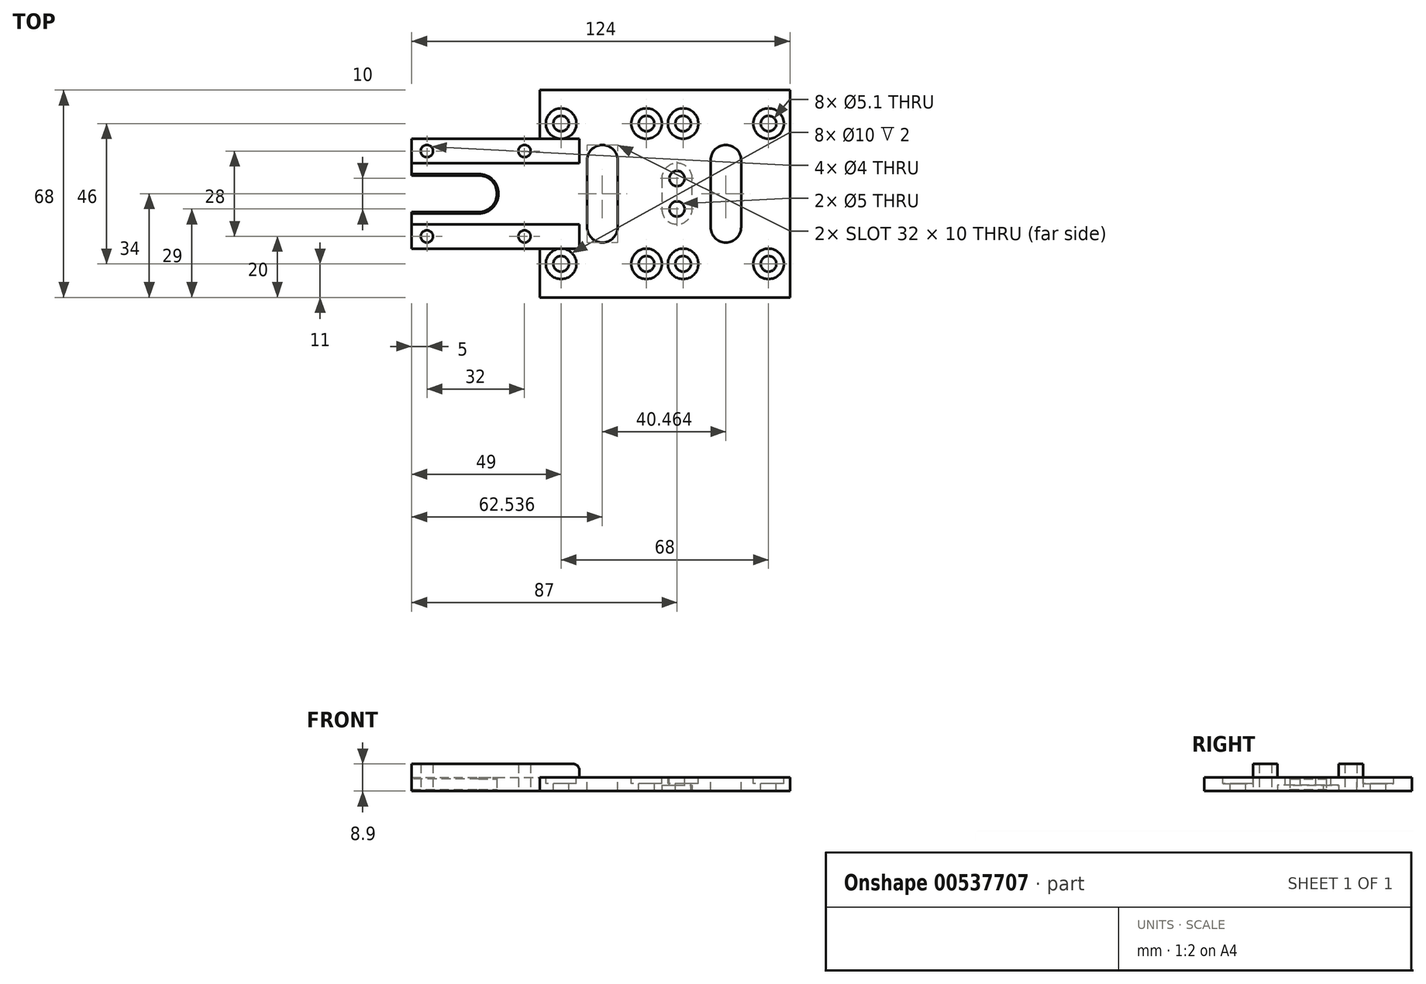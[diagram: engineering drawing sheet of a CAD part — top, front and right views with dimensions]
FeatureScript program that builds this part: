
annotation { "Feature Type Name" : "Feature", "Feature Type Description" : "" }
export const myFeature = defineFeature(function(context is Context, id is Id, definition is map)
    precondition{}
    {
        {
            var Q0;
            Q0=qCreatedBy(makeId("Top.planeOp"),FACE);
            var sketch = newSketch(context, id + "F0", { "sketchPlane" : qUnion([Q0])});
            skLineSegment(sketch, "E0.bottom", {"start": v(0, 0) * mm, "end": v(82, 0) * mm});
            skLineSegment(sketch, "E0.top", {"start": v(0, 68) * mm, "end": v(82, 68) * mm});
            skLineSegment(sketch, "E0.left", {"start": v(0, 0) * mm, "end": v(0, 16) * mm});
            skLineSegment(sketch, "E0.right", {"start": v(82, 0) * mm, "end": v(82, 68) * mm});
            skLineSegment(sketch, "E1.bottom", {"start": v(0, 52) * mm, "end": v(-42, 52) * mm});
            skLineSegment(sketch, "E1.top", {"start": v(0, 16) * mm, "end": v(-42, 16) * mm});
            skLineSegment(sketch, "E1.right", {"start": v(-42, 52) * mm, "end": v(-42, 40) * mm});
            skArc(sketch, "E2", {"start": v(-20.02, 28) * mm, "mid": v(-14.02, 34) * mm, "end": v(-20.02, 40) * mm});
            skLineSegment(sketch, "E3.bottom", {"start": v(-20.02, 40) * mm, "end": v(-42, 40) * mm});
            skLineSegment(sketch, "E3.top", {"start": v(-20.02, 28) * mm, "end": v(-42, 28) * mm});
            skLineSegment(sketch, "E3.left", {"start": v(-20.02, 28) * mm, "end": v(-20.02, 28) * mm});
            skLineSegment(sketch, "E4.trimOffspring", {"start": v(0, 52) * mm, "end": v(0, 68) * mm});
            skLineSegment(sketch, "E5.trimOffspring", {"start": v(-42, 28) * mm, "end": v(-42, 16) * mm});
            skSolve(sketch);
        }
        {
            var Q0;
            Q0=makeQuery(id+"F0.imprint","IMPRINT",FACE,{"disambiguationData":[TD([[makeQuery(id+"F0.imprint","IMPRINT",EDGE,{"derivedFrom":sQuery(id+"F0.wireOp",EDGE,"E0.bottom")}),1.0]])]});
            extrude(context, id + "F1", {"entities" : qUnion([Q0]), "depth" : 4.5 * mm, "offsetDistance" : 25 * mm});
        }
        {
            var Q0;
            Q0=makeQuery(id+"F1.opExtrude","CAP_FACE",FACE,{"disambiguationData":[OSD([sQuery(id+"F0.wireOp",EDGE,"E0.bottom"),sQuery(id+"F0.wireOp",EDGE,"E0.top"),sQuery(id+"F0.wireOp",EDGE,"E0.left"),sQuery(id+"F0.wireOp",EDGE,"E0.right"),sQuery(id+"F0.wireOp",EDGE,"E1.bottom"),sQuery(id+"F0.wireOp",EDGE,"E1.top"),sQuery(id+"F0.wireOp",EDGE,"E1.right"),sQuery(id+"F0.wireOp",EDGE,"E2"),sQuery(id+"F0.wireOp",EDGE,"E3.bottom"),sQuery(id+"F0.wireOp",EDGE,"E3.top"),sQuery(id+"F0.wireOp",EDGE,"E3.left"),sQuery(id+"F0.wireOp",EDGE,"E4.trimOffspring"),sQuery(id+"F0.wireOp",EDGE,"E5.trimOffspring")])],"isStart":false});
            var sketch = newSketch(context, id + "F2", { "sketchPlane" : qUnion([Q0])});
            skCircle(sketch, "E6", {"center": v(75, 57) * mm, "radius": 2.55 * mm});
            skCircle(sketch, "E7", {"center": v(75, 11) * mm, "radius": 2.55 * mm});
            skCircle(sketch, "E8", {"center": v(47, 57) * mm, "radius": 2.55 * mm});
            skCircle(sketch, "E9", {"center": v(47, 11) * mm, "radius": 2.55 * mm});
            skCircle(sketch, "E10", {"center": v(35, 57) * mm, "radius": 2.55 * mm});
            skCircle(sketch, "E11", {"center": v(35, 11) * mm, "radius": 2.55 * mm});
            skCircle(sketch, "E12", {"center": v(7, 57) * mm, "radius": 2.55 * mm});
            skCircle(sketch, "E13", {"center": v(7, 11) * mm, "radius": 2.55 * mm});
            skSolve(sketch);
        }
        {
            var Q0;
            Q0 = qSketchRegion(id + "F2", true);
            extrude(context, id + "F3", {"entities" : qUnion([Q0]), "operationType" : NewBodyOperationType.REMOVE, "oppositeDirection" : true, "depth" : 25 * mm, "offsetDistance" : 25 * mm});
        }
        {
            var Q0;
            Q0=makeQuery(id+"F1.opExtrude","CAP_FACE",FACE,{"disambiguationData":[OSD([sQuery(id+"F0.wireOp",EDGE,"E0.bottom"),sQuery(id+"F0.wireOp",EDGE,"E0.top"),sQuery(id+"F0.wireOp",EDGE,"E0.left"),sQuery(id+"F0.wireOp",EDGE,"E0.right"),sQuery(id+"F0.wireOp",EDGE,"E1.bottom"),sQuery(id+"F0.wireOp",EDGE,"E1.top"),sQuery(id+"F0.wireOp",EDGE,"E1.right"),sQuery(id+"F0.wireOp",EDGE,"E2"),sQuery(id+"F0.wireOp",EDGE,"E3.bottom"),sQuery(id+"F0.wireOp",EDGE,"E3.top"),sQuery(id+"F0.wireOp",EDGE,"E3.left"),sQuery(id+"F0.wireOp",EDGE,"E4.trimOffspring"),sQuery(id+"F0.wireOp",EDGE,"E5.trimOffspring")])],"isStart":false});
            var sketch = newSketch(context, id + "F4", { "sketchPlane" : qUnion([Q0])});
            skLineSegment(sketch, "E14.bottom", {"start": v(-42, 52) * mm, "end": v(13, 52) * mm});
            skLineSegment(sketch, "E14.top", {"start": v(-42, 44) * mm, "end": v(13, 44) * mm});
            skLineSegment(sketch, "E14.left", {"start": v(-42, 52) * mm, "end": v(-42, 44) * mm});
            skLineSegment(sketch, "E14.right", {"start": v(13, 52) * mm, "end": v(13, 44) * mm});
            skPoint(sketch, "E15.oppositeSnap0", {"position": v(-45, 24) * mm});
            skLineSegment(sketch, "E15.bottom", {"start": v(-42, 16) * mm, "end": v(13, 16) * mm});
            skLineSegment(sketch, "E15.top", {"start": v(-42, 24) * mm, "end": v(13, 24) * mm});
            skLineSegment(sketch, "E15.left", {"start": v(-42, 16) * mm, "end": v(-42, 24) * mm});
            skLineSegment(sketch, "E15.right", {"start": v(13, 16) * mm, "end": v(13, 24) * mm});
            skSolve(sketch);
        }
        {
            var Q0;
            Q0 = qSketchRegion(id + "F4", true);
            extrude(context, id + "F5", {"entities" : qUnion([Q0]), "operationType" : NewBodyOperationType.ADD, "depth" : 4.4 * mm, "offsetDistance" : 25 * mm});
        }
        {
            var Q0;
            {var subQ2=sQuery(id+"F0.wireOp",EDGE,"E5.trimOffspring");var subQ3=sQuery(id+"F0.wireOp",EDGE,"E3.left");var subQ4=sQuery(id+"F0.wireOp",EDGE,"E3.top");var subQ5=sQuery(id+"F0.wireOp",EDGE,"E0.right");var subQ6=sQuery(id+"F0.wireOp",EDGE,"E3.bottom");var subQ7=sQuery(id+"F0.wireOp",EDGE,"E1.right");var subQ8=sQuery(id+"F0.wireOp",EDGE,"E2");Q0=makeQuery(id+"F5.boolean.opBoolean","SPLIT",FACE,{"disambiguationData":[TD([makeQuery(id+"F1.opExtrude","SWEPT_FACE",FACE,{"disambiguationData":[OSD([subQ7])]})])],"derivedFrom":makeQuery(id+"F1.opExtrude","CAP_FACE",FACE,{"disambiguationData":[OSD([sQuery(id+"F0.wireOp",EDGE,"E0.bottom"),sQuery(id+"F0.wireOp",EDGE,"E0.top"),sQuery(id+"F0.wireOp",EDGE,"E0.left"),subQ5,sQuery(id+"F0.wireOp",EDGE,"E1.bottom"),sQuery(id+"F0.wireOp",EDGE,"E1.top"),subQ7,subQ8,subQ6,subQ4,subQ3,sQuery(id+"F0.wireOp",EDGE,"E4.trimOffspring"),subQ2])],"isStart":false})});}
            var sketch = newSketch(context, id + "F6", { "sketchPlane" : qUnion([Q0])});
            skCircle(sketch, "E16", {"center": v(45, 29) * mm, "radius": 2.5 * mm});
            skCircle(sketch, "E17", {"center": v(45, 39) * mm, "radius": 2.5 * mm});
            skSolve(sketch);
        }
        {
            var Q0;
            Q0 = qSketchRegion(id + "F6", true);
            extrude(context, id + "F7", {"entities" : qUnion([Q0]), "operationType" : NewBodyOperationType.REMOVE, "oppositeDirection" : true, "depth" : 25 * mm, "offsetDistance" : 25 * mm});
        }
        {
            var Q0;
            Q0=makeQuery(id+"F1.opExtrude","CAP_FACE",FACE,{"disambiguationData":[OSD([sQuery(id+"F0.wireOp",EDGE,"E0.bottom"),sQuery(id+"F0.wireOp",EDGE,"E0.top"),sQuery(id+"F0.wireOp",EDGE,"E0.left"),sQuery(id+"F0.wireOp",EDGE,"E0.right"),sQuery(id+"F0.wireOp",EDGE,"E1.bottom"),sQuery(id+"F0.wireOp",EDGE,"E1.top"),sQuery(id+"F0.wireOp",EDGE,"E1.right"),sQuery(id+"F0.wireOp",EDGE,"E2"),sQuery(id+"F0.wireOp",EDGE,"E3.bottom"),sQuery(id+"F0.wireOp",EDGE,"E3.top"),sQuery(id+"F0.wireOp",EDGE,"E4.trimOffspring"),sQuery(id+"F0.wireOp",EDGE,"E5.trimOffspring")])],"isStart":true});
            var sketch = newSketch(context, id + "F8", { "sketchPlane" : qUnion([Q0])});
            skCircle(sketch, "E18", {"center": v(-37, -48) * mm, "radius": 2 * mm});
            skCircle(sketch, "E19", {"center": v(-5, -48) * mm, "radius": 2 * mm});
            skCircle(sketch, "E20", {"center": v(-37, -20) * mm, "radius": 2 * mm});
            skCircle(sketch, "E21", {"center": v(-5, -20) * mm, "radius": 2 * mm});
            skSolve(sketch);
        }
        {
            var Q0;
            Q0 = qSketchRegion(id + "F8", true);
            extrude(context, id + "F9", {"entities" : qUnion([Q0]), "operationType" : NewBodyOperationType.REMOVE, "oppositeDirection" : true, "depth" : 25 * mm, "offsetDistance" : 25 * mm});
        }
        {
            var Q0;
            Q0=makeQuery(id+"F1.opExtrude","CAP_FACE",FACE,{"disambiguationData":[OSD([sQuery(id+"F0.wireOp",EDGE,"E0.bottom"),sQuery(id+"F0.wireOp",EDGE,"E0.top"),sQuery(id+"F0.wireOp",EDGE,"E0.left"),sQuery(id+"F0.wireOp",EDGE,"E0.right"),sQuery(id+"F0.wireOp",EDGE,"E1.bottom"),sQuery(id+"F0.wireOp",EDGE,"E1.top"),sQuery(id+"F0.wireOp",EDGE,"E1.right"),sQuery(id+"F0.wireOp",EDGE,"E2"),sQuery(id+"F0.wireOp",EDGE,"E3.bottom"),sQuery(id+"F0.wireOp",EDGE,"E3.top"),sQuery(id+"F0.wireOp",EDGE,"E4.trimOffspring"),sQuery(id+"F0.wireOp",EDGE,"E5.trimOffspring")])],"isStart":false});
            var sketch = newSketch(context, id + "F10", { "sketchPlane" : qUnion([Q0])});
            skLineSegment(sketch, "E22.bottom", {"start": v(56, 50) * mm, "end": v(66, 50) * mm});
            skLineSegment(sketch, "E22.top", {"start": v(56, 18) * mm, "end": v(66, 18) * mm});
            skLineSegment(sketch, "E22.left", {"start": v(56, 50) * mm, "end": v(56, 18) * mm});
            skLineSegment(sketch, "E22.right", {"start": v(66, 50) * mm, "end": v(66, 18) * mm});
            skLineSegment(sketch, "E23.bottom", {"start": v(15.54, 50) * mm, "end": v(25.54, 50) * mm});
            skLineSegment(sketch, "E23.top", {"start": v(15.54, 18) * mm, "end": v(25.54, 18) * mm});
            skLineSegment(sketch, "E23.left", {"start": v(15.54, 50) * mm, "end": v(15.54, 18) * mm});
            skLineSegment(sketch, "E23.right", {"start": v(25.54, 50) * mm, "end": v(25.54, 18) * mm});
            skSolve(sketch);
        }
        {
            var Q0;
            Q0 = qSketchRegion(id + "F10", true);
            extrude(context, id + "F11", {"entities" : qUnion([Q0]), "operationType" : NewBodyOperationType.REMOVE, "oppositeDirection" : true, "depth" : 25 * mm, "offsetDistance" : 25 * mm});
        }
        {
            var Q0;
            Q0=makeQuery(id+"F11.boolean.opBoolean","COPY",EDGE,{"derivedFrom":makeQuery(id+"F11.opExtrude","SWEPT_EDGE",EDGE,{"disambiguationData":[OSD([sQuery(id+"F4.wireOp",EDGE,"E14.right"),sQuery(id+"F10.wireOp",EDGE,"E23.bottom"),sQuery(id+"F10.wireOp",EDGE,"E23.left")])]})});
            var Q1;
            Q1=makeQuery(id+"F11.boolean.opBoolean","COPY",EDGE,{"derivedFrom":makeQuery(id+"F11.opExtrude","SWEPT_EDGE",EDGE,{"disambiguationData":[OSD([sQuery(id+"F10.wireOp",EDGE,"E23.bottom"),sQuery(id+"F10.wireOp",EDGE,"E23.right")])]})});
            var Q2;
            Q2=makeQuery(id+"F11.boolean.opBoolean","COPY",EDGE,{"derivedFrom":makeQuery(id+"F11.opExtrude","SWEPT_EDGE",EDGE,{"disambiguationData":[OSD([sQuery(id+"F4.wireOp",EDGE,"E15.right"),sQuery(id+"F10.wireOp",EDGE,"E23.top"),sQuery(id+"F10.wireOp",EDGE,"E23.left")])]})});
            var Q3;
            Q3=makeQuery(id+"F11.boolean.opBoolean","COPY",EDGE,{"derivedFrom":makeQuery(id+"F11.opExtrude","SWEPT_EDGE",EDGE,{"disambiguationData":[OSD([sQuery(id+"F10.wireOp",EDGE,"E23.top"),sQuery(id+"F10.wireOp",EDGE,"E23.right")])]})});
            fillet(context, id + "F12", {"entities" : qUnion([Q0, Q1, Q2, Q3]), "radius" : 5 * mm, "tangentPropagation" : true, "allowEdgeOverflow" : false});
        }
        {
            var Q0;
            Q0=makeQuery(id+"F11.boolean.opBoolean","COPY",EDGE,{"derivedFrom":makeQuery(id+"F11.opExtrude","SWEPT_EDGE",EDGE,{"disambiguationData":[OSD([sQuery(id+"F10.wireOp",EDGE,"E22.top"),sQuery(id+"F10.wireOp",EDGE,"E22.left")])]})});
            var Q1;
            Q1=makeQuery(id+"F11.boolean.opBoolean","COPY",EDGE,{"derivedFrom":makeQuery(id+"F11.opExtrude","SWEPT_EDGE",EDGE,{"disambiguationData":[OSD([sQuery(id+"F10.wireOp",EDGE,"E22.top"),sQuery(id+"F10.wireOp",EDGE,"E22.right")])]})});
            var Q2;
            Q2=makeQuery(id+"F11.boolean.opBoolean","COPY",EDGE,{"derivedFrom":makeQuery(id+"F11.opExtrude","SWEPT_EDGE",EDGE,{"disambiguationData":[OSD([sQuery(id+"F10.wireOp",EDGE,"E22.bottom"),sQuery(id+"F10.wireOp",EDGE,"E22.right")])]})});
            var Q3;
            Q3=makeQuery(id+"F11.boolean.opBoolean","COPY",EDGE,{"derivedFrom":makeQuery(id+"F11.opExtrude","SWEPT_EDGE",EDGE,{"disambiguationData":[OSD([sQuery(id+"F10.wireOp",EDGE,"E22.bottom"),sQuery(id+"F10.wireOp",EDGE,"E22.left")])]})});
            fillet(context, id + "F13", {"entities" : qUnion([Q0, Q1, Q2, Q3]), "radius" : 5 * mm, "tangentPropagation" : true, "allowEdgeOverflow" : false});
        }
        {
            var Q0;
            Q0=makeQuery(id+"F5.opExtrude","CAP_EDGE",EDGE,{"disambiguationData":[OSD([sQuery(id+"F4.wireOp",EDGE,"E14.right")])],"isStart":false});
            var Q1;
            Q1=makeQuery(id+"F5.opExtrude","CAP_EDGE",EDGE,{"disambiguationData":[OSD([sQuery(id+"F4.wireOp",EDGE,"E15.right")])],"isStart":false});
            fillet(context, id + "F14", {"entities" : qUnion([Q0, Q1]), "radius" : 2 * mm, "tangentPropagation" : true, "allowEdgeOverflow" : false});
        }
        {
            var Q0;
            Q0=makeQuery(id+"F1.opExtrude","CAP_FACE",FACE,{"disambiguationData":[OSD([sQuery(id+"F0.wireOp",EDGE,"E0.bottom"),sQuery(id+"F0.wireOp",EDGE,"E0.top"),sQuery(id+"F0.wireOp",EDGE,"E0.left"),sQuery(id+"F0.wireOp",EDGE,"E0.right"),sQuery(id+"F0.wireOp",EDGE,"E1.bottom"),sQuery(id+"F0.wireOp",EDGE,"E1.top"),sQuery(id+"F0.wireOp",EDGE,"E1.right"),sQuery(id+"F0.wireOp",EDGE,"E2"),sQuery(id+"F0.wireOp",EDGE,"E3.bottom"),sQuery(id+"F0.wireOp",EDGE,"E3.top"),sQuery(id+"F0.wireOp",EDGE,"E4.trimOffspring"),sQuery(id+"F0.wireOp",EDGE,"E5.trimOffspring")])],"isStart":false});
            var sketch = newSketch(context, id + "F15", { "sketchPlane" : qUnion([Q0])});
            skCircle(sketch, "E24", {"center": v(75, 11) * mm, "radius": 5 * mm});
            skCircle(sketch, "E25", {"center": v(47, 11) * mm, "radius": 5 * mm});
            skCircle(sketch, "E26", {"center": v(35, 11) * mm, "radius": 5 * mm});
            skCircle(sketch, "E27", {"center": v(7, 11) * mm, "radius": 5 * mm});
            skCircle(sketch, "E28", {"center": v(7, 57) * mm, "radius": 5 * mm});
            skCircle(sketch, "E29", {"center": v(35, 57) * mm, "radius": 5 * mm});
            skCircle(sketch, "E30", {"center": v(47, 57) * mm, "radius": 5 * mm});
            skCircle(sketch, "E31", {"center": v(75, 57) * mm, "radius": 5 * mm});
            skSolve(sketch);
        }
        {
            var Q0;
            Q0 = qSketchRegion(id + "F15", true);
            extrude(context, id + "F16", {"entities" : qUnion([Q0]), "operationType" : NewBodyOperationType.REMOVE, "oppositeDirection" : true, "depth" : 2 * mm, "offsetDistance" : 25 * mm});
        }
        {
            var Q0;
            Q0=makeQuery(id+"F1.opExtrude","CAP_FACE",FACE,{"disambiguationData":[OSD([sQuery(id+"F0.wireOp",EDGE,"E0.bottom"),sQuery(id+"F0.wireOp",EDGE,"E0.top"),sQuery(id+"F0.wireOp",EDGE,"E0.left"),sQuery(id+"F0.wireOp",EDGE,"E0.right"),sQuery(id+"F0.wireOp",EDGE,"E1.bottom"),sQuery(id+"F0.wireOp",EDGE,"E1.top"),sQuery(id+"F0.wireOp",EDGE,"E1.right"),sQuery(id+"F0.wireOp",EDGE,"E2"),sQuery(id+"F0.wireOp",EDGE,"E3.bottom"),sQuery(id+"F0.wireOp",EDGE,"E3.top"),sQuery(id+"F0.wireOp",EDGE,"E4.trimOffspring"),sQuery(id+"F0.wireOp",EDGE,"E5.trimOffspring")])],"isStart":true});
            var sketch = newSketch(context, id + "F17", { "sketchPlane" : qUnion([Q0])});
            skArc(sketch, "E32", {"start": v(40, -38.91) * mm, "mid": v(44.96, -44) * mm, "end": v(50, -39) * mm});
            skArc(sketch, "E33", {"start": v(50, -29) * mm, "mid": v(45, -24) * mm, "end": v(40, -29) * mm});
            skLineSegment(sketch, "E34", {"start": v(40, -39.09) * mm, "end": v(40, -29) * mm});
            skLineSegment(sketch, "E35", {"start": v(50, -29) * mm, "end": v(50, -39) * mm});
            skSolve(sketch);
        }
        {
            var Q0;
            Q0 = qSketchRegion(id + "F17", true);
            extrude(context, id + "F18", {"entities" : qUnion([Q0]), "operationType" : NewBodyOperationType.REMOVE, "oppositeDirection" : true, "depth" : 2 * mm, "offsetDistance" : 25 * mm});
        }
        {
            var Q0;
            Q0=makeQuery(id+"F1.opExtrude","CAP_EDGE",EDGE,{"disambiguationData":[OSD([sQuery(id+"F0.wireOp",EDGE,"E3.top")])],"isStart":false});
            var Q1;
            Q1=makeQuery(id+"F1.opExtrude","CAP_EDGE",EDGE,{"disambiguationData":[OSD([sQuery(id+"F0.wireOp",EDGE,"E3.bottom")])],"isStart":false});
            var Q2;
            Q2=makeQuery(id+"F1.opExtrude","CAP_EDGE",EDGE,{"disambiguationData":[OSD([sQuery(id+"F0.wireOp",EDGE,"E2")])],"isStart":false});
            chamfer(context, id + "F19", {"entities" : qUnion([Q0, Q1, Q2]), "width" : 0.5 * mm, "tangentPropagation" : true});
        }
        {
            var Q0;
            Q0=makeQuery(id+"F1.opExtrude","CAP_EDGE",EDGE,{"disambiguationData":[OSD([sQuery(id+"F0.wireOp",EDGE,"E3.bottom")])],"isStart":true});
            var Q1;
            Q1=makeQuery(id+"F1.opExtrude","CAP_EDGE",EDGE,{"disambiguationData":[OSD([sQuery(id+"F0.wireOp",EDGE,"E3.top")])],"isStart":true});
            var Q2;
            Q2=makeQuery(id+"F1.opExtrude","CAP_EDGE",EDGE,{"disambiguationData":[OSD([sQuery(id+"F0.wireOp",EDGE,"E2")])],"isStart":true});
            chamfer(context, id + "F20", {"entities" : qUnion([Q0, Q1, Q2]), "width" : 0.5 * mm, "tangentPropagation" : true});
        }
        {
            var Q0;
            Q0 = qSketchRegion(id + "F8", true);
            extrude(context, id + "F21", {"entities" : qUnion([Q0]), "operationType" : NewBodyOperationType.REMOVE, "oppositeDirection" : true, "depth" : 25 * mm, "offsetDistance" : 25 * mm});
        }
    });
